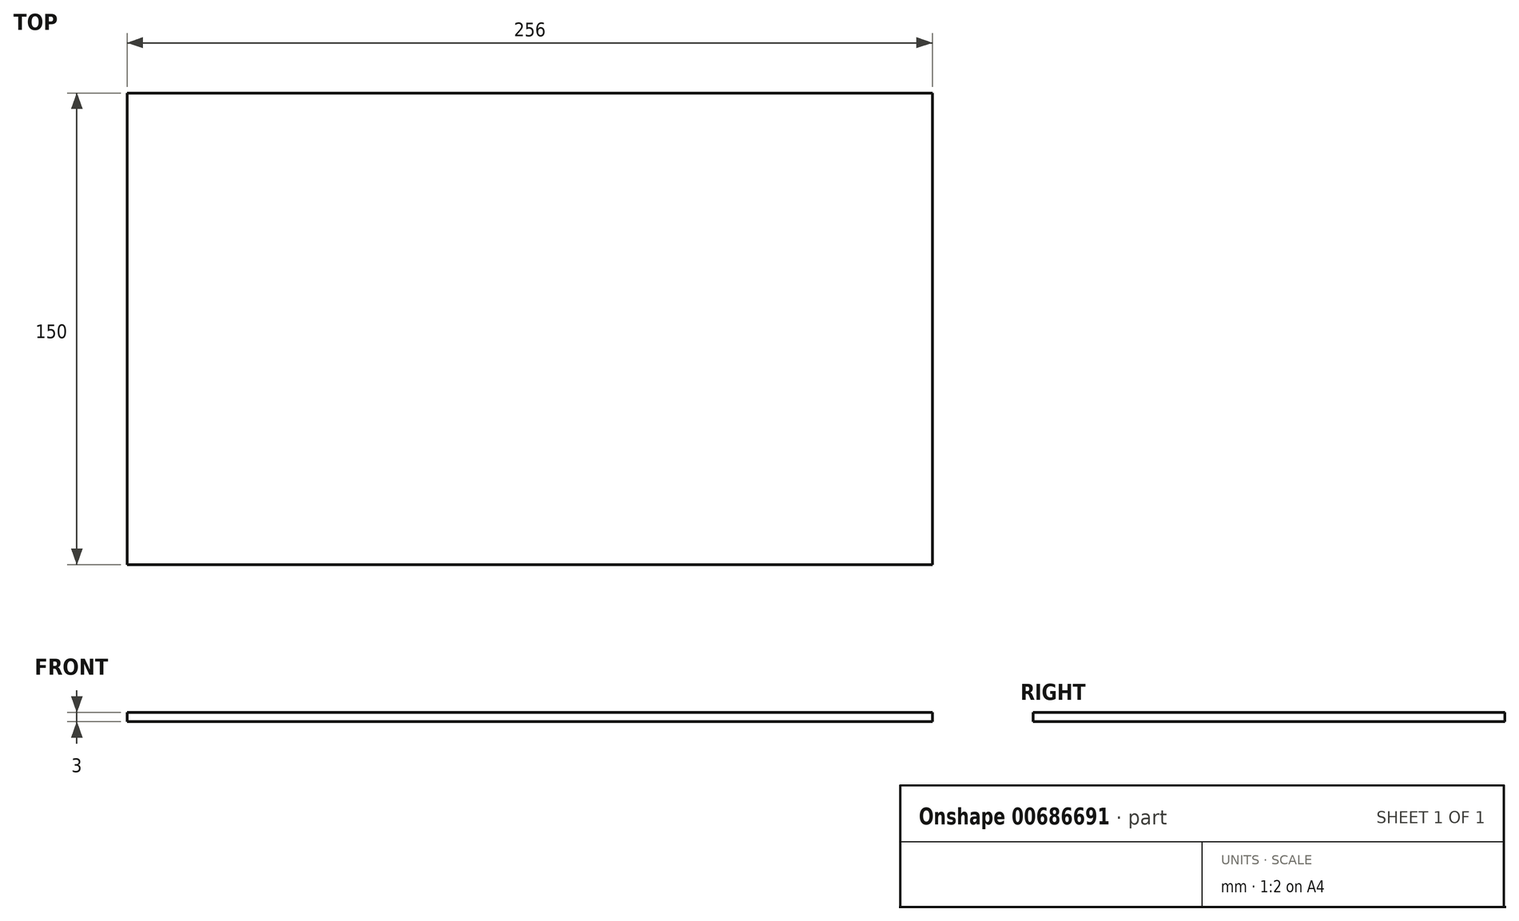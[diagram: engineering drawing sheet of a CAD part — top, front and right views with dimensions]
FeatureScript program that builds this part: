
annotation { "Feature Type Name" : "Feature", "Feature Type Description" : "" }
export const myFeature = defineFeature(function(context is Context, id is Id, definition is map)
    precondition{}
    {
        {
            var Q0;
            Q0=qCreatedBy(makeId("Top.planeOp"),FACE);
            var sketch = newSketch(context, id + "F0", { "sketchPlane" : qUnion([Q0])});
            skLineSegment(sketch, "E0.bottom", {"start": v(0, 0) * mm, "end": v(256, 0) * mm});
            skLineSegment(sketch, "E0.top", {"start": v(0, 150) * mm, "end": v(256, 150) * mm});
            skLineSegment(sketch, "E0.left", {"start": v(0, 0) * mm, "end": v(0, 150) * mm});
            skLineSegment(sketch, "E0.right", {"start": v(256, 0) * mm, "end": v(256, 150) * mm});
            skSolve(sketch);
        }
        {
            var Q0;
            Q0=makeQuery(id+"F0.imprint","IMPRINT",FACE,{"disambiguationData":[TD([[makeQuery(id+"F0.imprint","IMPRINT",EDGE,{"derivedFrom":sQuery(id+"F0.wireOp",EDGE,"E0.bottom")}),1.0]])]});
            extrude(context, id + "F1", {"entities" : qUnion([Q0]), "depth" : 3 * mm, "offsetDistance" : 25 * mm});
        }
    });
